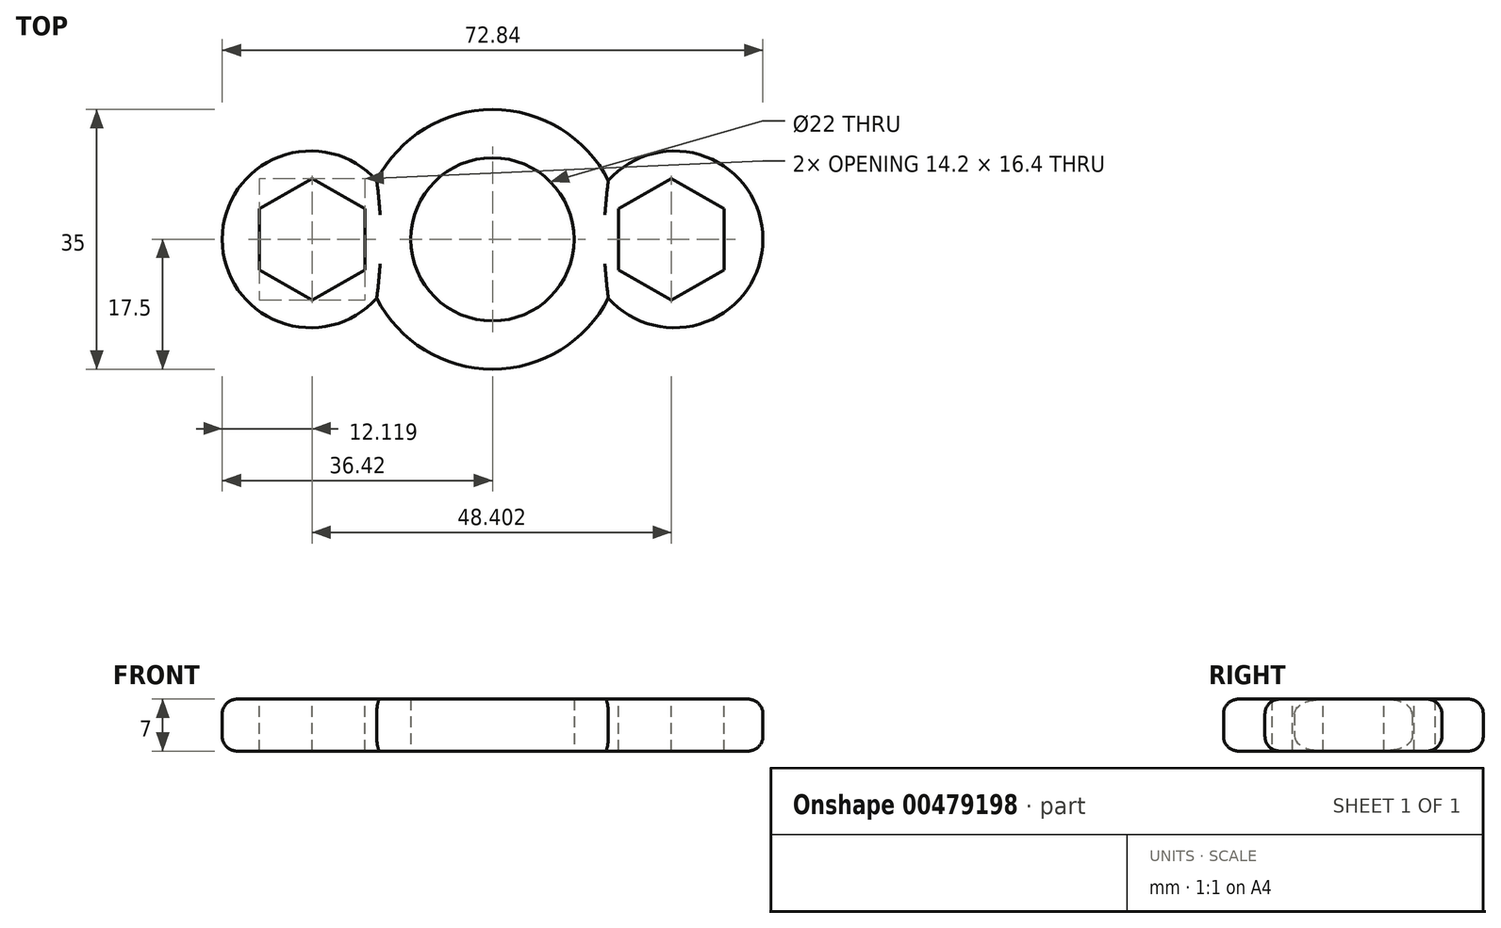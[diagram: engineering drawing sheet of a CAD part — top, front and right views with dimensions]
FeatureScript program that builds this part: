
annotation { "Feature Type Name" : "Feature", "Feature Type Description" : "" }
export const myFeature = defineFeature(function(context is Context, id is Id, definition is map)
    precondition{}
    {
        {
            var Q0;
            Q0=qCreatedBy(makeId("Top.planeOp"),FACE);
            var sketch = newSketch(context, id + "F0", { "sketchPlane" : qUnion([Q0])});
            skCircle(sketch, "E0", {"center": v(0, 0) * mm, "radius": 11 * mm});
            skCircle(sketch, "E1", {"center": v(0, 0) * mm, "radius": 17.5 * mm});
            skCircle(sketch, "E2", {"center": v(-24.5, 0) * mm, "radius": 11.92 * mm});
            skCircle(sketch, "E3", {"center": v(24.5, 0) * mm, "radius": 11.92 * mm});
            skLineSegment(sketch, "E4", {"start": v(-17.5, -6.25) * mm, "end": v(-16.35, -6.25) * mm});
            skLineSegment(sketch, "E5", {"start": v(-17.5, 6.25) * mm, "end": v(-16.35, 6.25) * mm});
            skLineSegment(sketch, "E6", {"start": v(17.5, -6.25) * mm, "end": v(16.35, -6.25) * mm});
            skLineSegment(sketch, "E7", {"start": v(17.5, 6.25) * mm, "end": v(16.35, 6.25) * mm});
            skLineSegment(sketch, "E8", {"start": v(-17.5, 6.25) * mm, "end": v(-19.35, 6.25) * mm});
            skLineSegment(sketch, "E9", {"start": v(-17.5, -6.25) * mm, "end": v(-19.35, -6.25) * mm});
            skLineSegment(sketch, "E10", {"start": v(17.5, 6.25) * mm, "end": v(19.35, 6.25) * mm});
            skLineSegment(sketch, "E11", {"start": v(17.5, -6.25) * mm, "end": v(19.35, -6.25) * mm});
            skSolve(sketch);
        }
        {
            var Q0;
            {var subQ0=sQuery(id+"F0.wireOp",EDGE,"E2");var subQ1=makeQuery(id+"F0.imprint","INTERSECT",VERTEX,{"derivedFrom":[subQ0,sQuery(id+"F0.wireOp",EDGE,"E8")]});Q0=makeQuery(id+"F0.imprint","IMPRINT",FACE,{"disambiguationData":[TD([[makeQuery(id+"F0.imprint","IMPRINT",EDGE,{"disambiguationData":[TD([[subQ1,-1.0]])],"derivedFrom":subQ0}),1.0]])]});}
            var Q1;
            {var subQ0=sQuery(id+"F0.wireOp",EDGE,"E3");var subQ1=makeQuery(id+"F0.imprint","INTERSECT",VERTEX,{"derivedFrom":[subQ0,sQuery(id+"F0.wireOp",EDGE,"E10")]});Q1=makeQuery(id+"F0.imprint","IMPRINT",FACE,{"disambiguationData":[TD([[makeQuery(id+"F0.imprint","IMPRINT",EDGE,{"disambiguationData":[TD([[subQ1,-1.0]])],"derivedFrom":subQ0}),1.0]])]});}
            var Q2;
            {var subQ1=sQuery(id+"F0.wireOp",EDGE,"E4");Q2=makeQuery(id+"F0.imprint","IMPRINT",FACE,{"disambiguationData":[TD([[makeQuery(id+"F0.imprint","IMPRINT",EDGE,{"derivedFrom":subQ1}),1.0]])]});}
            var Q3;
            {var subQ0=sQuery(id+"F0.wireOp",EDGE,"E6");Q3=makeQuery(id+"F0.imprint","IMPRINT",FACE,{"disambiguationData":[TD([[makeQuery(id+"F0.imprint","IMPRINT",EDGE,{"derivedFrom":subQ0}),-1.0]])]});}
            var Q4;
            Q4=makeQuery(id+"F0.imprint","IMPRINT",FACE,{"disambiguationData":[TD([[makeQuery(id+"F0.imprint","IMPRINT",EDGE,{"derivedFrom":sQuery(id+"F0.wireOp",EDGE,"E0")}),-1.0]])]});
            extrude(context, id + "F1", {"entities" : qUnion([Q0, Q1, Q2, Q3, Q4]), "depth" : 7 * mm});
        }
        {
            var Q0;
            Q0=makeQuery(id+"F1.opExtrude","CAP_FACE",FACE,{"disambiguationData":[OSD([sQuery(id+"F0.wireOp",EDGE,"E0"),sQuery(id+"F0.wireOp",EDGE,"E1"),sQuery(id+"F0.wireOp",EDGE,"E2"),sQuery(id+"F0.wireOp",EDGE,"E3"),sQuery(id+"F0.wireOp",EDGE,"Ul4fuTNM-kYAU-Hgel-qUKY-BZPXL3AtVHWM"),sQuery(id+"F0.wireOp",EDGE,"GSXVrAhl-FZuj-N8wU-qcgf-gdWxat4ashcG"),sQuery(id+"F0.wireOp",EDGE,"gsd28F3I-HgXZ-TJaw-tm29-ThQqYR4t14lY"),sQuery(id+"F0.wireOp",EDGE,"wtjfWSIm-jFJm-fzXd-6Ozm-R98YhWL6D4pz"),sQuery(id+"F0.wireOp",EDGE,"E4"),sQuery(id+"F0.wireOp",EDGE,"E5"),sQuery(id+"F0.wireOp",EDGE,"E6"),sQuery(id+"F0.wireOp",EDGE,"E7")])],"isStart":false});
            var sketch = newSketch(context, id + "F2", { "sketchPlane" : qUnion([Q0])});
            skLineSegment(sketch, "E12.0", {"start": v(-17.2, 4.1) * mm, "end": v(-17.2, -4.1) * mm});
            skLineSegment(sketch, "E12.1", {"start": v(-17.2, -4.1) * mm, "end": v(-24.3, -8.2) * mm});
            skLineSegment(sketch, "E12.2", {"start": v(-24.3, -8.2) * mm, "end": v(-31.4, -4.1) * mm});
            skLineSegment(sketch, "E12.3", {"start": v(-31.4, -4.1) * mm, "end": v(-31.4, 4.1) * mm});
            skLineSegment(sketch, "E12.4", {"start": v(-31.4, 4.1) * mm, "end": v(-24.3, 8.2) * mm});
            skLineSegment(sketch, "E12.5", {"start": v(-24.3, 8.2) * mm, "end": v(-17.2, 4.1) * mm});
            skPoint(sketch, "E12.0.midPoint", {"position": v(-27.9, 0) * mm});
            skLineSegment(sketch, "E13.0", {"start": v(31.2, 4.1) * mm, "end": v(31.2, -4.1) * mm});
            skLineSegment(sketch, "E13.1", {"start": v(31.2, -4.1) * mm, "end": v(24.1, -8.2) * mm});
            skLineSegment(sketch, "E13.2", {"start": v(24.1, -8.2) * mm, "end": v(17, -4.1) * mm});
            skLineSegment(sketch, "E13.3", {"start": v(17, -4.1) * mm, "end": v(17, 4.1) * mm});
            skLineSegment(sketch, "E13.4", {"start": v(17, 4.1) * mm, "end": v(24.1, 8.2) * mm});
            skLineSegment(sketch, "E13.5", {"start": v(24.1, 8.2) * mm, "end": v(31.2, 4.1) * mm});
            skPoint(sketch, "E13.0.midPoint", {"position": v(42.1, 0) * mm});
            skSolve(sketch);
        }
        {
            var Q0;
            Q0=makeQuery(id+"F2.imprint","IMPRINT",FACE,{"disambiguationData":[TD([[makeQuery(id+"F2.imprint","IMPRINT",EDGE,{"derivedFrom":sQuery(id+"F2.wireOp",EDGE,"E12.0")}),-1.0]])]});
            var Q1;
            Q1=makeQuery(id+"F2.imprint","IMPRINT",FACE,{"disambiguationData":[TD([[makeQuery(id+"F2.imprint","IMPRINT",EDGE,{"derivedFrom":sQuery(id+"F2.wireOp",EDGE,"E13.0")}),-1.0]])]});
            extrude(context, id + "F3", {"entities" : qUnion([Q0, Q1]), "operationType" : NewBodyOperationType.REMOVE, "endBound" : BoundingType.THROUGH_ALL, "oppositeDirection" : true, "depth" : 25 * mm});
        }
        {
            var Q0;
            {var subQ0=sQuery(id+"F0.wireOp",EDGE,"E1");Q0=makeQuery(id+"F1.opExtrude","CAP_EDGE",EDGE,{"disambiguationData":[OSD([subQ0]),TDD([makeQuery(id+"F0.imprint","IMPRINT",EDGE,{"disambiguationData":[TD([[makeQuery(id+"F0.imprint","INTERSECT",VERTEX,{"disambiguationData":[OD(1.0)],"derivedFrom":[subQ0,sQuery(id+"F0.wireOp",EDGE,"E2")]}),-1.0]])],"derivedFrom":subQ0})])],"isStart":false});}
            var Q1;
            Q1=makeQuery(id+"F1.opExtrude","CAP_EDGE",EDGE,{"disambiguationData":[OSD([sQuery(id+"F0.wireOp",EDGE,"E3")])],"isStart":false});
            var Q2;
            {var subQ0=sQuery(id+"F0.wireOp",EDGE,"E1");Q2=makeQuery(id+"F1.opExtrude","CAP_EDGE",EDGE,{"disambiguationData":[OSD([subQ0]),TDD([makeQuery(id+"F0.imprint","IMPRINT",EDGE,{"disambiguationData":[TD([[makeQuery(id+"F0.imprint","INTERSECT",VERTEX,{"disambiguationData":[OD(0.0)],"derivedFrom":[subQ0,sQuery(id+"F0.wireOp",EDGE,"E3")]}),-1.0]])],"derivedFrom":subQ0})])],"isStart":false});}
            var Q3;
            Q3=makeQuery(id+"F1.opExtrude","CAP_EDGE",EDGE,{"disambiguationData":[OSD([sQuery(id+"F0.wireOp",EDGE,"E2")])],"isStart":false});
            var Q4;
            {var subQ0=sQuery(id+"F0.wireOp",EDGE,"E1");Q4=makeQuery(id+"F1.opExtrude","CAP_EDGE",EDGE,{"disambiguationData":[OSD([subQ0]),TDD([makeQuery(id+"F0.imprint","IMPRINT",EDGE,{"disambiguationData":[TD([[makeQuery(id+"F0.imprint","INTERSECT",VERTEX,{"disambiguationData":[OD(1.0)],"derivedFrom":[subQ0,sQuery(id+"F0.wireOp",EDGE,"E2")]}),-1.0]])],"derivedFrom":subQ0})])],"isStart":true});}
            var Q5;
            {var subQ0=sQuery(id+"F0.wireOp",EDGE,"E1");Q5=makeQuery(id+"F1.opExtrude","CAP_EDGE",EDGE,{"disambiguationData":[OSD([subQ0]),TDD([makeQuery(id+"F0.imprint","IMPRINT",EDGE,{"disambiguationData":[TD([[makeQuery(id+"F0.imprint","INTERSECT",VERTEX,{"disambiguationData":[OD(0.0)],"derivedFrom":[subQ0,sQuery(id+"F0.wireOp",EDGE,"E3")]}),-1.0]])],"derivedFrom":subQ0})])],"isStart":true});}
            var Q6;
            Q6=makeQuery(id+"F1.opExtrude","CAP_EDGE",EDGE,{"disambiguationData":[OSD([sQuery(id+"F0.wireOp",EDGE,"E3")])],"isStart":true});
            var Q7;
            Q7=makeQuery(id+"F1.opExtrude","CAP_EDGE",EDGE,{"disambiguationData":[OSD([sQuery(id+"F0.wireOp",EDGE,"E2")])],"isStart":true});
            fillet(context, id + "F4", {"entities" : qUnion([Q0, Q1, Q2, Q3, Q4, Q5, Q6, Q7]), "radius" : 2 * mm, "tangentPropagation" : true, "allowEdgeOverflow" : false});
        }
    });
